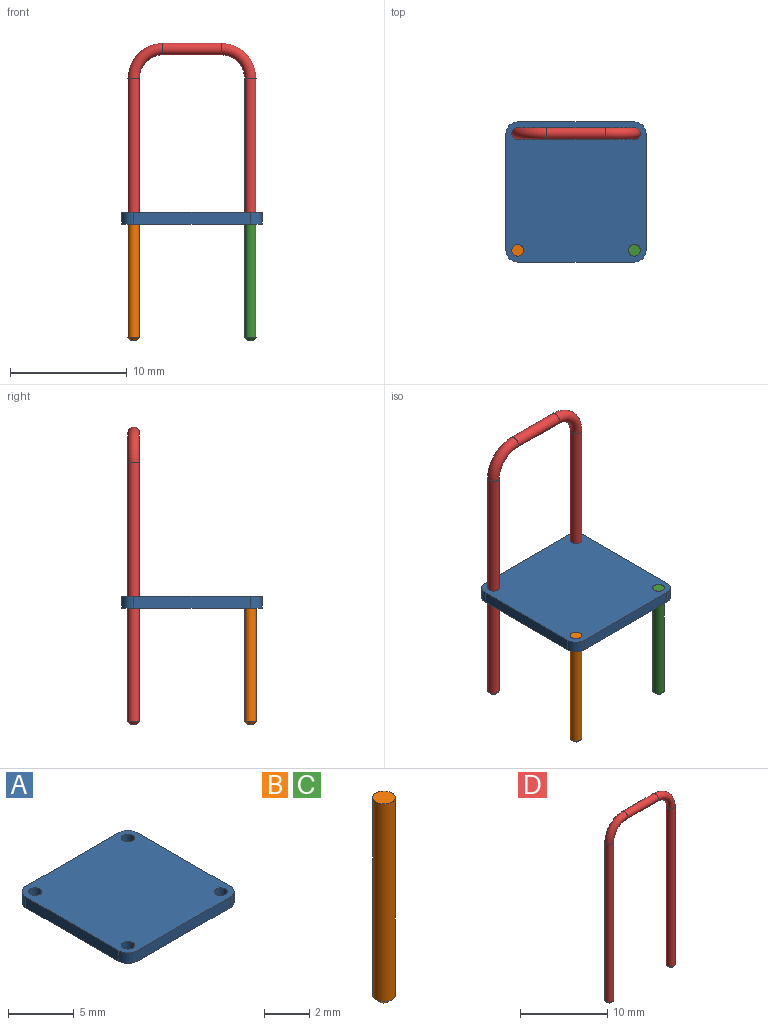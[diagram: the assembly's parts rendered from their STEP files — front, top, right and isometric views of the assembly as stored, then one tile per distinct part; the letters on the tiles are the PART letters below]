
ASSEMBLY  parts=4 mates=4
PART A: 14 faces, bbox 12x12x1 mm
  f0: plane 10x1mm, normal (0,-1,0), area 10mm2, adj f8,f9,f10,f13
  f1: plane 10x1mm, normal (1,0,0), area 10mm2, adj f8,f9,f10,f11
  f2: plane 10x1mm, normal (0,1,0), area 10mm2, adj f8,f9,f11,f12
  f3: cylinder r=0.5mm len=1mm, axis (0,0,-1), area 3.1mm2, adj f8,f9
  f4: cylinder r=0.5mm len=1mm, axis (0,0,-1), area 3.1mm2, adj f8,f9
  f5: cylinder r=0.5mm len=1mm, axis (0,0,-1), area 3.1mm2, adj f8,f9
  f6: cylinder r=0.5mm len=1mm, axis (0,0,-1), area 3.1mm2, adj f8,f9
  f7: plane 10x1mm, normal (-1,0,0), area 10mm2, adj f8,f9,f12,f13
  f8: plane 12x12mm, normal (0,0,1), area 140mm2, adj f0,f1,f2,f3,f4,f5,f6,f7
  f9: plane 12x12mm, normal (0,0,-1), area 140mm2, adj f0,f1,f2,f3,f4,f5,f6,f7
  f10: cylinder r=1mm len=1mm, axis (0,0,1), area 1.6mm2, adj f0,f1,f8,f9
  f11: cylinder r=1mm len=1mm, axis (0,0,-1), area 1.6mm2, adj f1,f2,f8,f9
  f12: cylinder r=1mm len=1mm, axis (0,0,1), area 1.6mm2, adj f2,f7,f8,f9
  f13: cylinder r=1mm len=1mm, axis (0,0,-1), area 1.6mm2, adj f0,f7,f8,f9
PART B: 4 faces, bbox 1x1x11 mm
  f0: plane 0.5x0.5mm, normal (0,0,-1), area 0.2mm2, adj f3
  f1: plane 1x1mm, normal (0,0,1), area 0.8mm2, adj f2
  f2: cylinder r=0.5mm len=10.75mm, axis (0,0,-1), area 33.8mm2, adj f1,f3
  f3: cone r=0.25mm half-angle=45deg, axis (0,0,1), area 0.8mm2, adj f0,f2
PART C: same geometry as B
PART D: 9 faces, bbox 11.5x1x25.7 mm
  f0: plane 0.5x0.5mm, normal (0,0,-1), area 0.2mm2, adj f7
  f1: plane 0.5x0.5mm, normal (0,0,-1), area 0.2mm2, adj f8
  f2: cylinder r=0.5mm len=22.25mm, axis (0,0,1), area 69.9mm2, adj f3,f7
  f3: torus R=2.5mm, axis (0,1,0), area 12.3mm2, adj f2,f4
  f4: cylinder r=0.5mm len=5mm, axis (1,0,0), area 15.7mm2, adj f3,f5
  f5: torus R=2.5mm, axis (0,1,0), area 12.3mm2, adj f4,f6
  f6: cylinder r=0.5mm len=22.25mm, axis (0,0,-1), area 69.9mm2, adj f5,f8
  f7: cone r=0.5mm half-angle=45deg, axis (0,0,1), area 0.8mm2, adj f0,f2
  f8: cone r=0.25mm half-angle=45deg, axis (0,0,1), area 0.8mm2, adj f1,f6
PLACE A t=(0.25,-0.04,-0.78)mm fixed
PLACE B rot(axis=(0,0,1),180deg) t=(-4.75,-5.04,-10.78)mm
PLACE C t=(5.25,-5.04,-10.78)mm
PLACE D t=(-4.75,4.96,-10.78)mm
MATE fastened A.f5 <-> B.f2  axis (0,0,1) through (-4.75,-5.04,0.22)mm
MATE planar D.f6 <-> C.f2  axis (0,0,-1) through (5.25,4.96,-10.78)mm
MATE fastened C.f2 <-> A.f4  axis (0,0,1) through (5.25,-5.04,0.22)mm
MATE slider D.f6 <-> A.f3  axis (0,0,-1) through (5.25,4.96,0.6)mm
